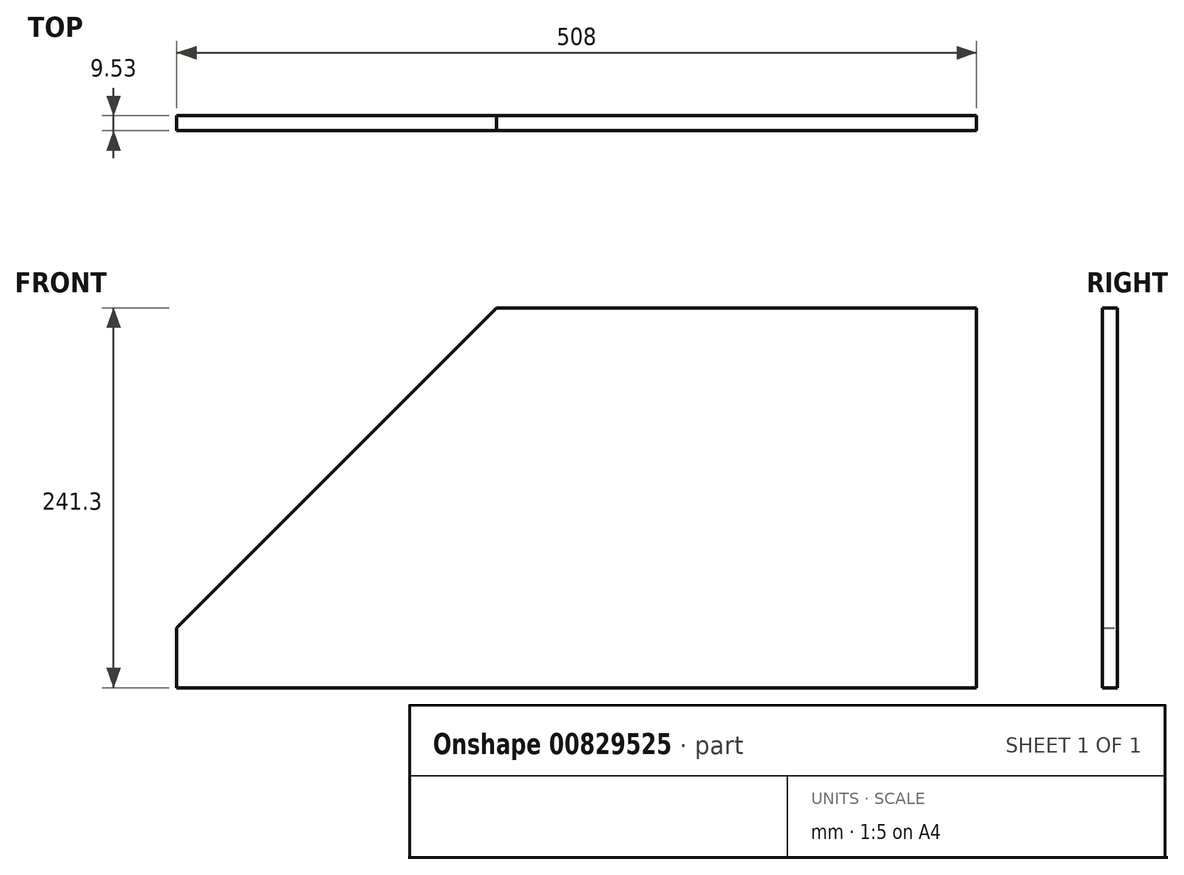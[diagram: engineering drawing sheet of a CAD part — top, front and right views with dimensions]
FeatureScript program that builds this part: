
annotation { "Feature Type Name" : "Feature", "Feature Type Description" : "" }
export const myFeature = defineFeature(function(context is Context, id is Id, definition is map)
    precondition{}
    {
        {
            var Q0;
            Q0=qCreatedBy(makeId("Front.planeOp"),FACE);
            var sketch = newSketch(context, id + "F0", { "sketchPlane" : qUnion([Q0])});
            skLineSegment(sketch, "E0.bottom", {"start": v(-254, -19.05) * mm, "end": v(254, -19.05) * mm});
            skLineSegment(sketch, "E0.left", {"start": v(-254, -19.05) * mm, "end": v(-254, 19.05) * mm});
            skPoint(sketch, "E0.middle", {"position": v(0, 0) * mm});
            skLineSegment(sketch, "E1", {"start": v(254, -19.05) * mm, "end": v(254, 222.25) * mm});
            skLineSegment(sketch, "E2", {"start": v(254, 222.25) * mm, "end": v(-50.8, 222.25) * mm});
            skLineSegment(sketch, "E3", {"start": v(-50.8, 222.25) * mm, "end": v(-254, 19.05) * mm});
            skSolve(sketch);
        }
        {
            var Q0;
            Q0 = qSketchRegion(id + "F0", true);
            extrude(context, id + "F1", {"entities" : qUnion([Q0]), "depth" : 9.52 * mm, "offsetDistance" : 25.4 * mm});
        }
    });
